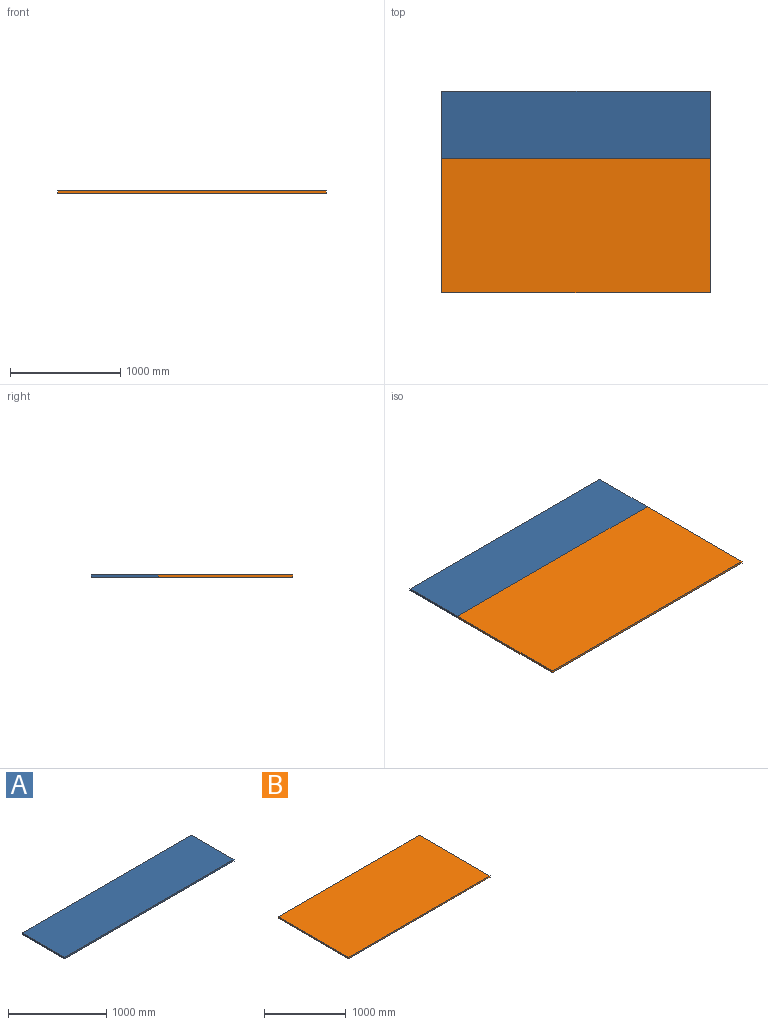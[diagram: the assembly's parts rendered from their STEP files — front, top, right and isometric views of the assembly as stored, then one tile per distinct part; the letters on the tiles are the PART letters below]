
ASSEMBLY  parts=2 mates=1
PART A: 6 faces, bbox 2438.4x609.6x19.1 mm
  f0: plane 2438.4x19.05mm, normal (0,-1,0), area 46451.5mm2, adj f1,f3,f4,f5
  f1: plane 609.6x19.05mm, normal (1,0,0), area 11612.9mm2, adj f0,f2,f4,f5
  f2: plane 2438.4x19.05mm, normal (0,1,0), area 46451.5mm2, adj f1,f3,f4,f5
  f3: plane 609.6x19.05mm, normal (-1,0,0), area 11612.9mm2, adj f0,f2,f4,f5
  f4: plane 2438.4x609.6mm, normal (0,0,1), area 1486448.6mm2, adj f0,f1,f2,f3
  f5: plane 2438.4x609.6mm, normal (0,0,-1), area 1486448.6mm2, adj f0,f1,f2,f3
PART B: 6 faces, bbox 2438.4x1219.2x19.1 mm
  f0: plane 1219.2x19.05mm, normal (1,0,0), area 23225.8mm2, adj f1,f3,f4,f5
  f1: plane 2438.4x19.05mm, normal (0,1,0), area 46451.5mm2, adj f0,f2,f4,f5
  f2: plane 1219.2x19.05mm, normal (-1,0,0), area 23225.8mm2, adj f1,f3,f4,f5
  f3: plane 2438.4x19.05mm, normal (0,-1,0), area 46451.5mm2, adj f0,f2,f4,f5
  f4: plane 2438.4x1219.2mm, normal (0,0,1), area 2972897.3mm2, adj f0,f1,f2,f3
  f5: plane 2438.4x1219.2mm, normal (0,0,-1), area 2972897.3mm2, adj f0,f1,f2,f3
PLACE A t=(0,914.4,-19.05)mm
PLACE B t=(0,0,-19.05)mm
MATE fastened B.f4 <-> A.f4  axis (0,0,1) through (1219.2,609.6,0)mm
